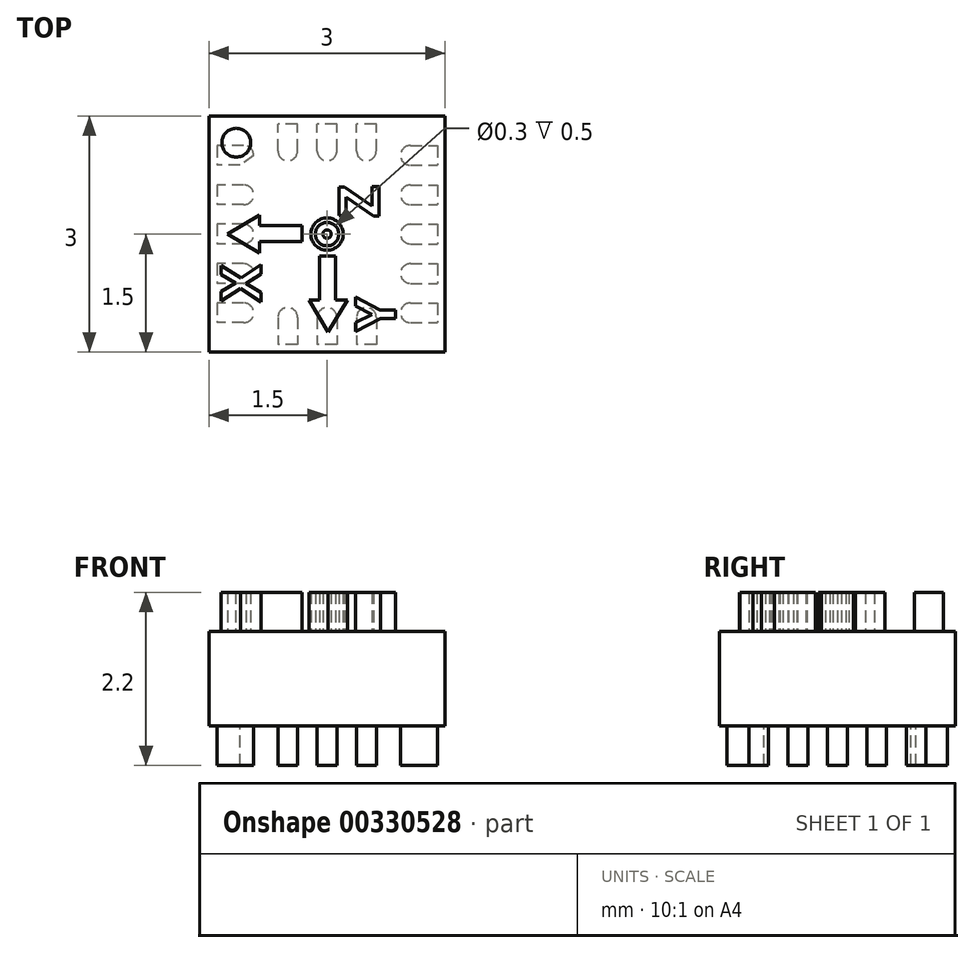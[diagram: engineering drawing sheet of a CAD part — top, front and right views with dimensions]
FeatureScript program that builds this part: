
annotation { "Feature Type Name" : "Feature", "Feature Type Description" : "" }
export const myFeature = defineFeature(function(context is Context, id is Id, definition is map)
    precondition{}
    {
        {
            var Q0;
            Q0=qCreatedBy(makeId("Top.planeOp"),FACE);
            var sketch = newSketch(context, id + "F0", { "sketchPlane" : qUnion([Q0])});
            skLineSegment(sketch, "E0.bottom", {"start": v(1.5, -1.5) * mm, "end": v(-1.5, -1.5) * mm});
            skLineSegment(sketch, "E0.top", {"start": v(1.5, 1.5) * mm, "end": v(-1.5, 1.5) * mm});
            skLineSegment(sketch, "E0.left", {"start": v(1.5, -1.5) * mm, "end": v(1.5, 1.5) * mm});
            skLineSegment(sketch, "E0.right", {"start": v(-1.5, -1.5) * mm, "end": v(-1.5, 1.5) * mm});
            skPoint(sketch, "E0.middle", {"position": v(0, 0) * mm});
            skSolve(sketch);
        }
        {
            var Q0;
            Q0 = qSketchRegion(id + "F0", true);
            extrude(context, id + "F1", {"entities" : qUnion([Q0]), "depth" : 1.2 * mm, "offsetDistance" : 25 * mm});
        }
        {
            var Q0;
            Q0=makeQuery(id+"F1.opExtrude","CAP_FACE",FACE,{"disambiguationData":[OSD([sQuery(id+"F0.wireOp",EDGE,"E0.bottom"),sQuery(id+"F0.wireOp",EDGE,"E0.top"),sQuery(id+"F0.wireOp",EDGE,"E0.left"),sQuery(id+"F0.wireOp",EDGE,"E0.right")])],"isStart":false});
            var sketch = newSketch(context, id + "F2", { "sketchPlane" : qUnion([Q0])});
            skCircle(sketch, "E1", {"center": v(-1.15, 1.16) * mm, "radius": 0.18 * mm});
            skLineSegment(sketch, "E2.bottom", {"start": v(-0.32, 0.11) * mm, "end": v(-0.86, 0.11) * mm});
            skLineSegment(sketch, "E2.top", {"start": v(-0.32, -0.1) * mm, "end": v(-0.86, -0.1) * mm});
            skLineSegment(sketch, "E2.left", {"start": v(-0.32, 0.11) * mm, "end": v(-0.32, -0.1) * mm});
            skLineSegment(sketch, "E3", {"start": v(-0.86, 0.11) * mm, "end": v(-0.86, 0.24) * mm});
            skLineSegment(sketch, "E4", {"start": v(-0.86, 0.24) * mm, "end": v(-1.26, 0) * mm});
            skLineSegment(sketch, "E5", {"start": v(-1.26, 0) * mm, "end": v(-0.86, -0.24) * mm});
            skLineSegment(sketch, "E6", {"start": v(-0.86, -0.24) * mm, "end": v(-0.86, -0.1) * mm});
            skText(sketch, "E7", { "text": "X", "fontName": "OpenSans-Bold.ttf"});
            skLineSegment(sketch, "E8.bottom", {"start": v(-0.1, -0.28) * mm, "end": v(-0.1, -0.84) * mm});
            skLineSegment(sketch, "E8.top", {"start": v(0.1, -0.28) * mm, "end": v(0.1, -0.84) * mm});
            skLineSegment(sketch, "E8.left", {"start": v(-0.1, -0.28) * mm, "end": v(0.1, -0.28) * mm});
            skLineSegment(sketch, "E9", {"start": v(-0.1, -0.84) * mm, "end": v(-0.23, -0.84) * mm});
            skLineSegment(sketch, "E10", {"start": v(-0.23, -0.84) * mm, "end": v(0.01, -1.24) * mm});
            skLineSegment(sketch, "E11", {"start": v(0.01, -1.24) * mm, "end": v(0.26, -0.84) * mm});
            skLineSegment(sketch, "E12", {"start": v(0.26, -0.84) * mm, "end": v(0.1, -0.84) * mm});
            skText(sketch, "E13", { "text": "Y", "fontName": "OpenSans-Bold.ttf"});
            skCircle(sketch, "E14", {"center": v(0, 0) * mm, "radius": 0.2 * mm});
            skCircle(sketch, "E15", {"center": v(0, 0) * mm, "radius": 0.15 * mm});
            skText(sketch, "E16", { "text": "Z\n", "fontName": "OpenSans-Bold.ttf"});
            const initialGuessF2  = {"E7": [-0.00084, -0.00086, 0, 1, 0.00051], "E13": [0.00087, -0.00124, 0, 1, 0.00051], "E16": [0.00066, 0.00021, 0, 1, 0.00051]};
            skSetInitialGuess(sketch, initialGuessF2);
            skSolve(sketch);
        }
        {
            var Q0;
            Q0 = qSketchRegion(id + "F2", true);
            extrude(context, id + "F3", {"entities" : qUnion([Q0]), "depth" : .5 * mm, "offsetDistance" : 25 * mm});
        }
        {
            var Q0;
            Q0=makeQuery(id+"F1.opExtrude","CAP_FACE",FACE,{"disambiguationData":[OSD([sQuery(id+"F0.wireOp",EDGE,"E0.bottom"),sQuery(id+"F0.wireOp",EDGE,"E0.top"),sQuery(id+"F0.wireOp",EDGE,"E0.left"),sQuery(id+"F0.wireOp",EDGE,"E0.right")])],"isStart":true});
            var sketch = newSketch(context, id + "F4", { "sketchPlane" : qUnion([Q0])});
            skLineSegment(sketch, "E17", {"start": v(0, 1.5) * mm, "end": v(0, -1.5) * mm, "construction": true});
            skLineSegment(sketch, "E18", {"start": v(-1.5, 0) * mm, "end": v(1.5, 0) * mm, "construction": true});
            skLineSegment(sketch, "E19.bottom", {"start": v(-1.06, 0.88) * mm, "end": v(-1.4, 0.88) * mm});
            skLineSegment(sketch, "E19.top", {"start": v(-1.06, 1.13) * mm, "end": v(-1.4, 1.13) * mm});
            skLineSegment(sketch, "E19.right", {"start": v(-1.4, 0.88) * mm, "end": v(-1.4, 1.12) * mm});
            skPoint(sketch, "E19.middle", {"position": v(-1.23, 1) * mm});
            skArc(sketch, "E20", {"start": v(-1.06, 1.12) * mm, "mid": v(-0.93, 1) * mm, "end": v(-1.06, 0.88) * mm});
            skArc(sketch, "E21.0.1.0", {"start": v(-1.06, 0.62) * mm, "mid": v(-0.93, 0.5) * mm, "end": v(-1.06, 0.37) * mm});
            skLineSegment(sketch, "E21.0.1.1", {"start": v(-1.06, 0.63) * mm, "end": v(-1.4, 0.63) * mm});
            skLineSegment(sketch, "E21.0.1.2", {"start": v(-1.4, 0.38) * mm, "end": v(-1.4, 0.62) * mm});
            skPoint(sketch, "E21.0.1.3", {"position": v(-1.23, 0.5) * mm});
            skLineSegment(sketch, "E21.0.1.4", {"start": v(-1.06, 0.38) * mm, "end": v(-1.4, 0.38) * mm});
            skArc(sketch, "E21.0.2.0", {"start": v(-1.06, 0.12) * mm, "mid": v(-0.93, 0) * mm, "end": v(-1.06, -0.13) * mm});
            skLineSegment(sketch, "E21.0.2.1", {"start": v(-1.06, 0.13) * mm, "end": v(-1.4, 0.13) * mm});
            skLineSegment(sketch, "E21.0.2.2", {"start": v(-1.4, -0.12) * mm, "end": v(-1.4, 0.12) * mm});
            skPoint(sketch, "E21.0.2.3", {"position": v(-1.23, 0) * mm});
            skLineSegment(sketch, "E21.0.2.4", {"start": v(-1.06, -0.12) * mm, "end": v(-1.4, -0.13) * mm});
            skArc(sketch, "E21.0.3.0", {"start": v(-1.06, -0.38) * mm, "mid": v(-0.93, -0.5) * mm, "end": v(-1.06, -0.63) * mm});
            skLineSegment(sketch, "E21.0.3.1", {"start": v(-1.06, -0.37) * mm, "end": v(-1.4, -0.37) * mm});
            skLineSegment(sketch, "E21.0.3.2", {"start": v(-1.4, -0.62) * mm, "end": v(-1.4, -0.38) * mm});
            skPoint(sketch, "E21.0.3.3", {"position": v(-1.23, -0.5) * mm});
            skLineSegment(sketch, "E21.0.3.4", {"start": v(-1.06, -0.62) * mm, "end": v(-1.4, -0.62) * mm});
            skArc(sketch, "E21.0.4.0", {"start": v(-0.93, -1) * mm, "mid": v(-0.97, -1.09) * mm, "end": v(-1.06, -1.13) * mm});
            skLineSegment(sketch, "E21.0.4.1", {"start": v(-1.1, -0.87) * mm, "end": v(-1.4, -0.87) * mm});
            skLineSegment(sketch, "E21.0.4.2", {"start": v(-1.4, -1.13) * mm, "end": v(-1.4, -0.88) * mm});
            skPoint(sketch, "E21.0.4.3", {"position": v(-1.23, -1) * mm});
            skLineSegment(sketch, "E21.0.4.4", {"start": v(-1.06, -1.13) * mm, "end": v(-1.4, -1.13) * mm});
            skLineSegment(sketch, "E21.direction1", {"start": v(-1.4, 0.88) * mm, "end": v(1.9, 0.88) * mm, "construction": true});
            skLineSegment(sketch, "E21.direction2", {"start": v(-1.4, 0.88) * mm, "end": v(-1.4, 0.38) * mm, "construction": true});
            skLineSegment(sketch, "E22.MirrorCS", {"start": v(1.4, 0.38) * mm, "end": v(1.4, 0.62) * mm});
            skLineSegment(sketch, "E23.MirrorCS", {"start": v(1.06, 0.88) * mm, "end": v(1.4, 0.88) * mm});
            skLineSegment(sketch, "E24.MirrorCS", {"start": v(1.06, -0.62) * mm, "end": v(1.4, -0.62) * mm});
            skLineSegment(sketch, "E25.MirrorCS", {"start": v(1.06, -0.87) * mm, "end": v(1.4, -0.87) * mm});
            skLineSegment(sketch, "E26.MirrorCS", {"start": v(1.06, -1.13) * mm, "end": v(1.4, -1.13) * mm});
            skPoint(sketch, "E27.MirrorP", {"position": v(1.23, 0.5) * mm});
            skPoint(sketch, "E28.MirrorP", {"position": v(1.23, 0) * mm});
            skArc(sketch, "E29.MirrorCS", {"start": v(1.06, -0.88) * mm, "mid": v(0.93, -1) * mm, "end": v(1.06, -1.13) * mm});
            skPoint(sketch, "E30.MirrorP", {"position": v(1.23, -1) * mm});
            skLineSegment(sketch, "E31.MirrorCS", {"start": v(1.4, -0.12) * mm, "end": v(1.4, 0.12) * mm});
            skLineSegment(sketch, "E32.MirrorCS", {"start": v(1.06, 0.13) * mm, "end": v(1.4, 0.13) * mm});
            skLineSegment(sketch, "E33.MirrorCS", {"start": v(1.4, -1.13) * mm, "end": v(1.4, -0.88) * mm});
            skArc(sketch, "E34.MirrorCS", {"start": v(1.06, 0.12) * mm, "mid": v(0.93, 0) * mm, "end": v(1.06, -0.13) * mm});
            skLineSegment(sketch, "E35.MirrorCS", {"start": v(1.06, 0.38) * mm, "end": v(1.4, 0.38) * mm});
            skLineSegment(sketch, "E36.MirrorCS", {"start": v(1.4, 0.88) * mm, "end": v(-1.9, 0.88) * mm, "construction": true});
            skPoint(sketch, "E37.MirrorP", {"position": v(1.23, 1) * mm});
            skLineSegment(sketch, "E38.MirrorCS", {"start": v(1.06, 0.63) * mm, "end": v(1.4, 0.63) * mm});
            skLineSegment(sketch, "E39.MirrorCS", {"start": v(1.4, 0.88) * mm, "end": v(1.4, 0.38) * mm, "construction": true});
            skArc(sketch, "E40.MirrorCS", {"start": v(1.06, 0.62) * mm, "mid": v(0.93, 0.5) * mm, "end": v(1.06, 0.37) * mm});
            skArc(sketch, "E41.MirrorCS", {"start": v(1.06, 1.13) * mm, "mid": v(0.93, 1) * mm, "end": v(1.06, 0.88) * mm});
            skLineSegment(sketch, "E42.MirrorCS", {"start": v(1.4, 0.88) * mm, "end": v(1.4, 1.13) * mm});
            skLineSegment(sketch, "E43.MirrorCS", {"start": v(1.06, 1.13) * mm, "end": v(1.4, 1.13) * mm});
            skLineSegment(sketch, "E44.MirrorCS", {"start": v(1.5, 0) * mm, "end": v(-1.5, 0) * mm, "construction": true});
            skLineSegment(sketch, "E45.MirrorCS", {"start": v(1.06, -0.37) * mm, "end": v(1.4, -0.37) * mm});
            skArc(sketch, "E46.MirrorCS", {"start": v(1.06, -0.38) * mm, "mid": v(0.93, -0.5) * mm, "end": v(1.06, -0.63) * mm});
            skLineSegment(sketch, "E47.MirrorCS", {"start": v(1.4, -0.62) * mm, "end": v(1.4, -0.38) * mm});
            skLineSegment(sketch, "E48.MirrorCS", {"start": v(1.06, -0.12) * mm, "end": v(1.4, -0.12) * mm});
            skPoint(sketch, "E49.MirrorP", {"position": v(1.23, -0.5) * mm});
            skLineSegment(sketch, "E50.bottom", {"start": v(-0.38, 1.06) * mm, "end": v(-0.63, 1.06) * mm});
            skLineSegment(sketch, "E50.top", {"start": v(-0.38, 1.4) * mm, "end": v(-0.63, 1.4) * mm});
            skLineSegment(sketch, "E50.left", {"start": v(-0.38, 1.06) * mm, "end": v(-0.38, 1.4) * mm});
            skLineSegment(sketch, "E50.right", {"start": v(-0.63, 1.06) * mm, "end": v(-0.63, 1.4) * mm});
            skPoint(sketch, "E50.middle", {"position": v(-0.5, 1.23) * mm});
            skArc(sketch, "E51", {"start": v(-0.63, 1.06) * mm, "mid": v(-0.5, 0.93) * mm, "end": v(-0.38, 1.06) * mm});
            skLineSegment(sketch, "E52.1.0.0", {"start": v(1.9, 0.88) * mm, "end": v(-1.4, 0.88) * mm, "construction": true});
            skLineSegment(sketch, "E52.1.0.1", {"start": v(0.12, 1.06) * mm, "end": v(-0.13, 1.06) * mm});
            skLineSegment(sketch, "E52.1.0.2", {"start": v(0.12, 1.4) * mm, "end": v(-0.13, 1.4) * mm});
            skLineSegment(sketch, "E52.1.0.3", {"start": v(-0.13, 1.06) * mm, "end": v(-0.13, 1.4) * mm});
            skPoint(sketch, "E52.1.0.4", {"position": v(0, 1.23) * mm});
            skLineSegment(sketch, "E52.1.0.5", {"start": v(0.12, 1.06) * mm, "end": v(0.12, 1.4) * mm});
            skArc(sketch, "E52.1.0.6", {"start": v(-0.13, 1.06) * mm, "mid": v(0, 0.93) * mm, "end": v(0.12, 1.06) * mm});
            skLineSegment(sketch, "E52.1.0.7", {"start": v(-0.9, 0.88) * mm, "end": v(2.4, 0.88) * mm, "construction": true});
            skLineSegment(sketch, "E52.2.0.0", {"start": v(2.4, 0.88) * mm, "end": v(-0.9, 0.88) * mm, "construction": true});
            skLineSegment(sketch, "E52.2.0.1", {"start": v(0.62, 1.06) * mm, "end": v(0.37, 1.06) * mm});
            skLineSegment(sketch, "E52.2.0.2", {"start": v(0.62, 1.4) * mm, "end": v(0.37, 1.4) * mm});
            skLineSegment(sketch, "E52.2.0.3", {"start": v(0.37, 1.06) * mm, "end": v(0.37, 1.4) * mm});
            skPoint(sketch, "E52.2.0.4", {"position": v(0.5, 1.23) * mm});
            skLineSegment(sketch, "E52.2.0.5", {"start": v(0.62, 1.06) * mm, "end": v(0.62, 1.4) * mm});
            skArc(sketch, "E52.2.0.6", {"start": v(0.37, 1.06) * mm, "mid": v(0.5, 0.93) * mm, "end": v(0.62, 1.06) * mm});
            skLineSegment(sketch, "E52.2.0.7", {"start": v(-0.4, 0.88) * mm, "end": v(2.9, 0.88) * mm, "construction": true});
            skLineSegment(sketch, "E52.direction1", {"start": v(-1.9, 0.88) * mm, "end": v(-1.4, 0.88) * mm, "construction": true});
            skArc(sketch, "E53.MirrorCS", {"start": v(-0.13, -1.06) * mm, "mid": v(0, -0.93) * mm, "end": v(0.12, -1.06) * mm});
            skLineSegment(sketch, "E54.MirrorCS", {"start": v(-0.63, -1.06) * mm, "end": v(-0.63, -1.4) * mm});
            skArc(sketch, "E55.MirrorCS", {"start": v(-0.63, -1.06) * mm, "mid": v(-0.5, -0.93) * mm, "end": v(-0.38, -1.06) * mm});
            skPoint(sketch, "E56.MirrorP", {"position": v(-0.5, -1.23) * mm});
            skLineSegment(sketch, "E57.MirrorCS", {"start": v(-0.38, -1.06) * mm, "end": v(-0.63, -1.06) * mm});
            skLineSegment(sketch, "E58.MirrorCS", {"start": v(0.12, -1.4) * mm, "end": v(-0.13, -1.4) * mm});
            skLineSegment(sketch, "E59.MirrorCS", {"start": v(-0.38, -1.06) * mm, "end": v(-0.38, -1.4) * mm});
            skLineSegment(sketch, "E60.MirrorCS", {"start": v(0.62, -1.4) * mm, "end": v(0.37, -1.4) * mm});
            skLineSegment(sketch, "E61.MirrorCS", {"start": v(0.12, -1.06) * mm, "end": v(-0.13, -1.06) * mm});
            skLineSegment(sketch, "E62.MirrorCS", {"start": v(0.62, -1.06) * mm, "end": v(0.37, -1.06) * mm});
            skArc(sketch, "E63.MirrorCS", {"start": v(0.37, -1.06) * mm, "mid": v(0.5, -0.93) * mm, "end": v(0.62, -1.06) * mm});
            skPoint(sketch, "E64.MirrorP", {"position": v(0, -1.23) * mm});
            skLineSegment(sketch, "E65.MirrorCS", {"start": v(0.37, -1.06) * mm, "end": v(0.37, -1.4) * mm});
            skPoint(sketch, "E66.MirrorP", {"position": v(0.5, -1.23) * mm});
            skLineSegment(sketch, "E67.MirrorCS", {"start": v(0, -1.5) * mm, "end": v(0, 1.5) * mm, "construction": true});
            skLineSegment(sketch, "E68.MirrorCS", {"start": v(-0.13, -1.06) * mm, "end": v(-0.13, -1.4) * mm});
            skLineSegment(sketch, "E69.MirrorCS", {"start": v(-0.38, -1.4) * mm, "end": v(-0.63, -1.4) * mm});
            skLineSegment(sketch, "E70.MirrorCS", {"start": v(0.62, -1.06) * mm, "end": v(0.62, -1.4) * mm});
            skLineSegment(sketch, "E71.MirrorCS", {"start": v(0.12, -1.06) * mm, "end": v(0.12, -1.4) * mm});
            skLineSegment(sketch, "E72", {"start": v(-0.93, -1) * mm, "end": v(-1.1, -0.87) * mm});
            skPoint(sketch, "E73.orphan", {"position": v(-1.06, -0.87) * mm});
            skSolve(sketch);
        }
        {
            var Q0;
            Q0 = qSketchRegion(id + "F4", true);
            extrude(context, id + "F5", {"entities" : qUnion([Q0]), "depth" : .5 * mm, "offsetDistance" : 25 * mm});
        }
        {
            var Q0;
            Q0=makeQuery(id+"F2.imprint","IMPRINT",FACE,{"disambiguationData":[TD([[makeQuery(id+"F2.imprint","IMPRINT",EDGE,{"derivedFrom":sQuery(id+"F2.wireOp",EDGE,"E15")}),1.0]])]});
            var sketch = newSketch(context, id + "F6", { "sketchPlane" : qUnion([Q0])});
            skCircle(sketch, "E74", {"center": v(0, 0) * mm, "radius": 0.05 * mm});
            skSolve(sketch);
        }
        {
            var Q0;
            Q0 = qSketchRegion(id + "F6", true);
            extrude(context, id + "F7", {"entities" : qUnion([Q0]), "depth" : .5 * mm, "offsetDistance" : 25 * mm});
        }
    });
